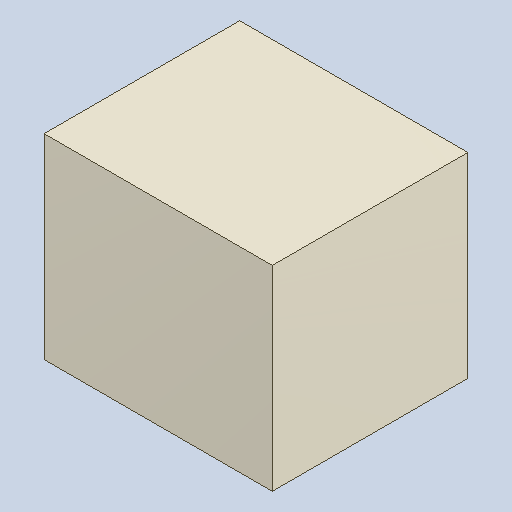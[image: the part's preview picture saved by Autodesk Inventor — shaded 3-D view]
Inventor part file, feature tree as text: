
AUTODESK INVENTOR PART (.ipt)
format: ipt  version: 2023.4 (Build 274418000, 418)  size: 82,432 bytes
history: native  units: mm
features: extrude x1
ambient origin geometry x8: Origin, YZ Plane, XZ Plane, XY Plane, X Axis, Y Axis, Z Axis, Center Point
bodies: Solid1 (feature_tree)
feature tree (1):
  extrude  "Extruded_9"  [1 undecoded]
note: 1 required parameter value undecoded (feature->parameter linkage not recoverable at this tier; creation-order binding heuristic only, values carry confidence <= 0.55)
